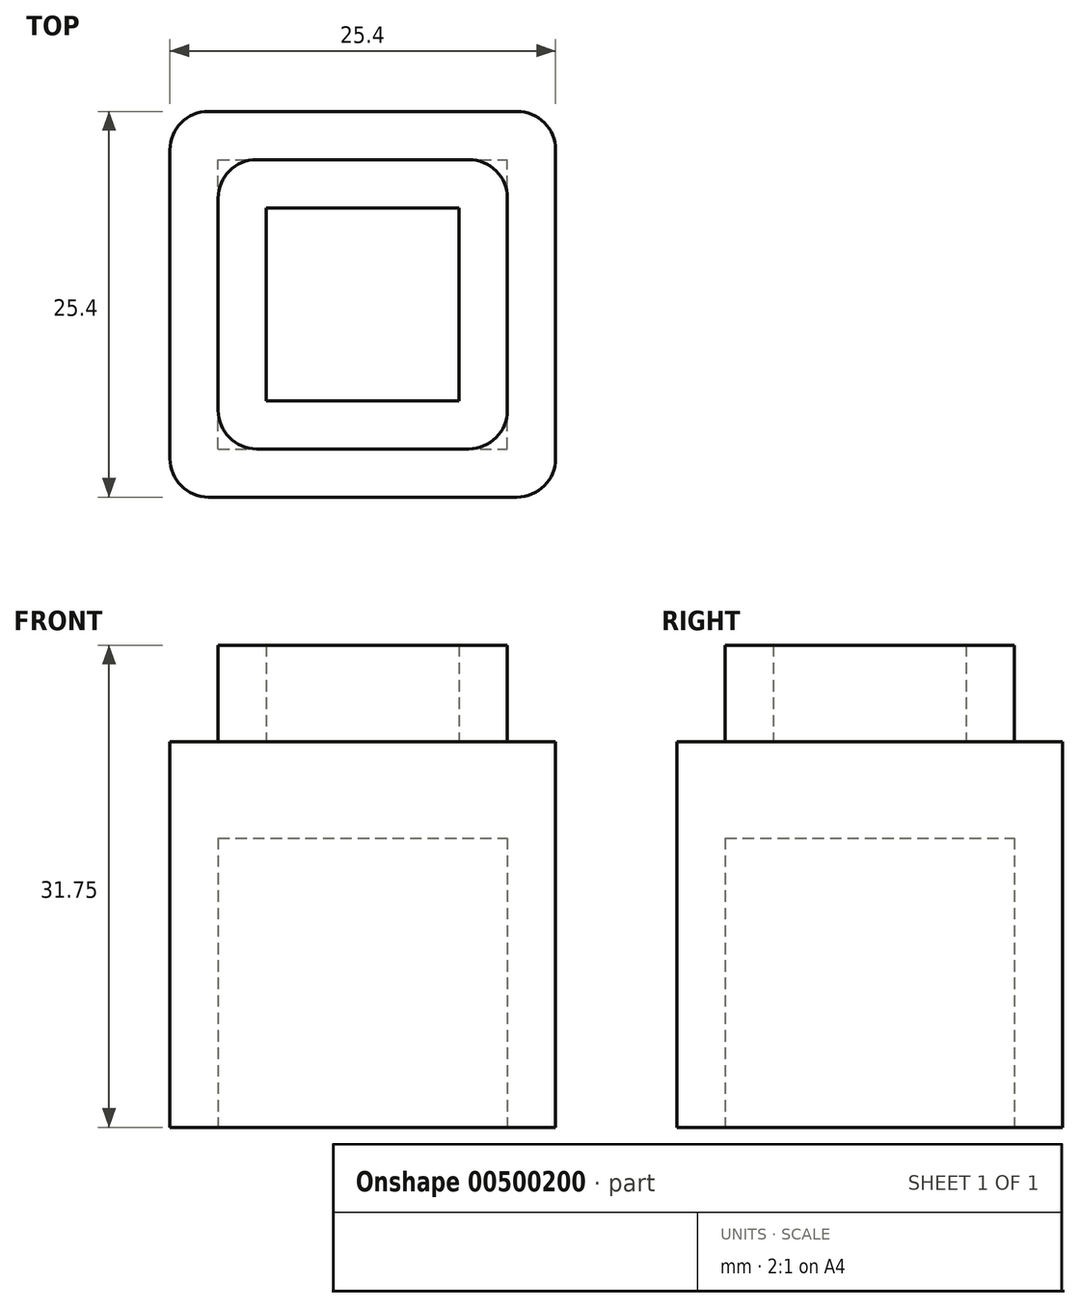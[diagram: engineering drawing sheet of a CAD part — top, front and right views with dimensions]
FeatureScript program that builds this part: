
annotation { "Feature Type Name" : "Feature", "Feature Type Description" : "" }
export const myFeature = defineFeature(function(context is Context, id is Id, definition is map)
    precondition{}
    {
        {
            var Q0;
            Q0=qCreatedBy(makeId("Top.planeOp"),FACE);
            var sketch = newSketch(context, id + "F0", { "sketchPlane" : qUnion([Q0])});
            skLineSegment(sketch, "E0.bottom", {"start": v(0, 0) * mm, "end": v(25.4, 0) * mm});
            skLineSegment(sketch, "E0.top", {"start": v(0, -25.4) * mm, "end": v(25.4, -25.4) * mm});
            skLineSegment(sketch, "E0.left", {"start": v(0, 0) * mm, "end": v(0, -25.4) * mm});
            skLineSegment(sketch, "E0.right", {"start": v(25.4, 0) * mm, "end": v(25.4, -25.4) * mm});
            skSolve(sketch);
        }
        {
            var Q0;
            Q0 = qSketchRegion(id + "F0", true);
            extrude(context, id + "F1", {"entities" : qUnion([Q0]), "depth" : 25.4 * mm});
        }
        {
            var Q0;
            Q0=makeQuery(id+"F1.opExtrude","CAP_FACE",FACE,{"disambiguationData":[OSD([sQuery(id+"F0.wireOp",EDGE,"E0.bottom"),sQuery(id+"F0.wireOp",EDGE,"E0.top"),sQuery(id+"F0.wireOp",EDGE,"E0.left"),sQuery(id+"F0.wireOp",EDGE,"E0.right")])],"isStart":true});
            var sketch = newSketch(context, id + "F2", { "sketchPlane" : qUnion([Q0])});
            skLineSegment(sketch, "E1", {"start": v(0, 0) * mm, "end": v(25.4, 25.4) * mm, "construction": true});
            skLineSegment(sketch, "E2.bottom", {"start": v(3.18, 22.23) * mm, "end": v(22.23, 22.23) * mm});
            skLineSegment(sketch, "E2.top", {"start": v(3.18, 3.18) * mm, "end": v(22.23, 3.18) * mm});
            skLineSegment(sketch, "E2.left", {"start": v(3.18, 22.23) * mm, "end": v(3.18, 3.18) * mm});
            skLineSegment(sketch, "E2.right", {"start": v(22.23, 22.23) * mm, "end": v(22.23, 3.18) * mm});
            skLineSegment(sketch, "E3", {"start": v(3.18, 22.23) * mm, "end": v(22.23, 3.18) * mm, "construction": true});
            skPoint(sketch, "E4", {"position": v(12.7, 12.7) * mm});
            skSolve(sketch);
        }
        {
            var Q0;
            Q0 = qSketchRegion(id + "F2", true);
            extrude(context, id + "F3", {"entities" : qUnion([Q0]), "operationType" : NewBodyOperationType.REMOVE, "oppositeDirection" : true, "depth" : 19.05 * mm, "offsetDistance" : 25.4 * mm});
        }
        {
            var Q0;
            Q0=makeQuery(id+"F1.opExtrude","CAP_FACE",FACE,{"disambiguationData":[OSD([sQuery(id+"F0.wireOp",EDGE,"E0.bottom"),sQuery(id+"F0.wireOp",EDGE,"E0.top"),sQuery(id+"F0.wireOp",EDGE,"E0.left"),sQuery(id+"F0.wireOp",EDGE,"E0.right")])],"isStart":false});
            var sketch = newSketch(context, id + "F4", { "sketchPlane" : qUnion([Q0])});
            skLineSegment(sketch, "E5.bottom", {"start": v(6.35, -19.05) * mm, "end": v(19.05, -19.05) * mm});
            skLineSegment(sketch, "E5.top", {"start": v(6.35, -6.35) * mm, "end": v(19.05, -6.35) * mm});
            skLineSegment(sketch, "E5.left", {"start": v(6.35, -19.05) * mm, "end": v(6.35, -6.35) * mm});
            skLineSegment(sketch, "E5.right", {"start": v(19.05, -19.05) * mm, "end": v(19.05, -6.35) * mm});
            skLineSegment(sketch, "E6.bottom", {"start": v(3.18, -22.22) * mm, "end": v(22.23, -22.22) * mm});
            skLineSegment(sketch, "E6.top", {"start": v(3.18, -3.17) * mm, "end": v(22.23, -3.17) * mm});
            skLineSegment(sketch, "E6.left", {"start": v(3.18, -22.22) * mm, "end": v(3.18, -3.17) * mm});
            skLineSegment(sketch, "E6.right", {"start": v(22.23, -22.22) * mm, "end": v(22.23, -3.17) * mm});
            skLineSegment(sketch, "E7", {"start": v(0, 0) * mm, "end": v(25.4, -25.4) * mm, "construction": true});
            skLineSegment(sketch, "E8", {"start": v(6.35, -6.35) * mm, "end": v(19.05, -19.05) * mm, "construction": true});
            skLineSegment(sketch, "E9", {"start": v(3.18, -22.22) * mm, "end": v(22.23, -3.17) * mm, "construction": true});
            skPoint(sketch, "E10", {"position": v(12.7, -12.7) * mm});
            skSolve(sketch);
        }
        {
            var Q0;
            Q0 = qSketchRegion(id + "F4", true);
            extrude(context, id + "F5", {"entities" : qUnion([Q0]), "operationType" : NewBodyOperationType.ADD, "depth" : 6.35 * mm});
        }
        {
            var Q0;
            Q0=makeQuery(id+"F1.opExtrude","SWEPT_EDGE",EDGE,{"disambiguationData":[OSD([sQuery(id+"F0.wireOp",EDGE,"E0.bottom"),sQuery(id+"F0.wireOp",EDGE,"E0.left")])]});
            var Q1;
            Q1=makeQuery(id+"F1.opExtrude","SWEPT_EDGE",EDGE,{"disambiguationData":[OSD([sQuery(id+"F0.wireOp",EDGE,"E0.top"),sQuery(id+"F0.wireOp",EDGE,"E0.left")])]});
            var Q2;
            Q2=makeQuery(id+"F1.opExtrude","SWEPT_EDGE",EDGE,{"disambiguationData":[OSD([sQuery(id+"F0.wireOp",EDGE,"E0.bottom"),sQuery(id+"F0.wireOp",EDGE,"E0.right")])]});
            var Q3;
            Q3=makeQuery(id+"F5.opExtrude","SWEPT_EDGE",EDGE,{"disambiguationData":[OSD([sQuery(id+"F4.wireOp",EDGE,"E6.top"),sQuery(id+"F4.wireOp",EDGE,"E6.left")])]});
            var Q4;
            Q4=makeQuery(id+"F5.opExtrude","SWEPT_EDGE",EDGE,{"disambiguationData":[OSD([sQuery(id+"F4.wireOp",EDGE,"E6.bottom"),sQuery(id+"F4.wireOp",EDGE,"E6.left")])]});
            var Q5;
            Q5=makeQuery(id+"F5.opExtrude","SWEPT_EDGE",EDGE,{"disambiguationData":[OSD([sQuery(id+"F4.wireOp",EDGE,"E6.top"),sQuery(id+"F4.wireOp",EDGE,"E6.right")])]});
            var Q6;
            Q6=makeQuery(id+"F5.opExtrude","SWEPT_EDGE",EDGE,{"disambiguationData":[OSD([sQuery(id+"F4.wireOp",EDGE,"E6.bottom"),sQuery(id+"F4.wireOp",EDGE,"E6.right")])]});
            var Q7;
            Q7=makeQuery(id+"F1.opExtrude","SWEPT_EDGE",EDGE,{"disambiguationData":[OSD([sQuery(id+"F0.wireOp",EDGE,"E0.top"),sQuery(id+"F0.wireOp",EDGE,"E0.right")])]});
            fillet(context, id + "F6", {"entities" : qUnion([Q0, Q1, Q2, Q3, Q4, Q5, Q6, Q7]), "radius" : 2.54 * mm, "tangentPropagation" : true, "allowEdgeOverflow" : false});
        }
    });
